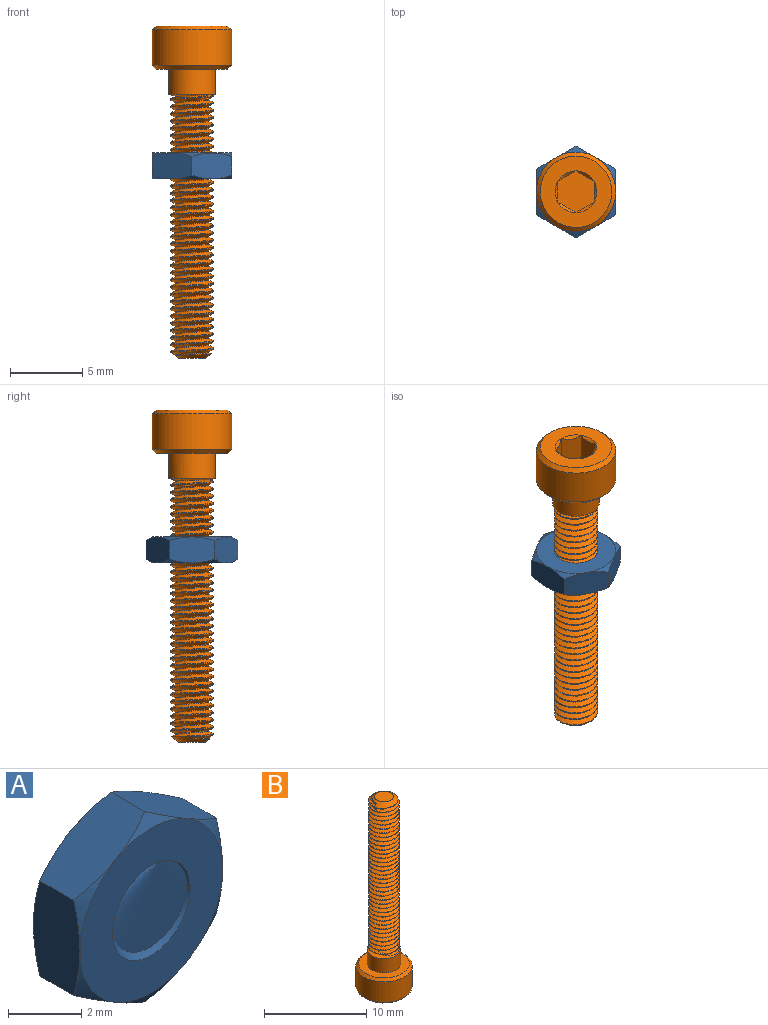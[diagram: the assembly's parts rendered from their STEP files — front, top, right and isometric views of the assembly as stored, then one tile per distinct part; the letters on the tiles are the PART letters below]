
ASSEMBLY  parts=2 mates=1
PART A: 26 faces, bbox 6.6x2.4x6.6 mm
  f0: bspline ~3.46x3mm, area 8.9mm2, adj f1,f11,f12,f19
  f1: bspline ~2.71x2.35mm, area 1.1mm2, adj f0,f2,f12,f19
  f2: bspline ~3.46x3mm, area 9.4mm2, adj f1,f11,f12,f19
  f3: plane 5.5x5.5mm, normal (0,1,0), area 16.7mm2, adj f11,f12,f13,f14,f15,f16,f17,f18
  f4: plane 3.01x2.07mm, normal (-0.5,0,-0.87), area 5.2mm2, adj f5,f9,f13,f18,f23,f24
  f5: plane 3.44x2.06mm, normal (-1,0,0), area 5.2mm2, adj f4,f6,f17,f18,f24,f25
  f6: plane 3.01x2.07mm, normal (-0.5,0,0.87), area 5.2mm2, adj f5,f7,f16,f17,f20,f25
  f7: plane 3.01x2.07mm, normal (0.5,0,0.87), area 5.2mm2, adj f6,f8,f15,f16,f20,f21
  f8: plane 3.44x2.06mm, normal (1,0,0), area 5.2mm2, adj f7,f9,f14,f15,f21,f22
  f9: plane 3.01x2.07mm, normal (0.5,0,-0.87), area 5.2mm2, adj f4,f8,f13,f14,f22,f23
  f10: plane 5.5x5.5mm, normal (0,-1,0), area 16.7mm2, adj f11,f19,f20,f21,f22,f23,f24,f25
  f11: cylinder r=1.5mm len=3mm, axis (0,-1,0), area 2.1mm2, adj f0,f2,f3,f10
  f12: cone r=1.5mm half-angle=45deg, axis (0,1,0), area 2mm2, adj f0,f1,f2,f3
  f13: cone r=2.75mm half-angle=60deg, axis (0,-1,0), area 0.7mm2, adj f3,f4,f9
  f14: cone r=2.75mm half-angle=60deg, axis (0,-1,0), area 0.7mm2, adj f3,f8,f9
  f15: cone r=2.75mm half-angle=60deg, axis (0,-1,0), area 0.7mm2, adj f3,f7,f8
  f16: cone r=2.75mm half-angle=60deg, axis (0,-1,0), area 0.7mm2, adj f3,f6,f7
  f17: cone r=2.75mm half-angle=60deg, axis (0,-1,0), area 0.7mm2, adj f3,f5,f6
  f18: cone r=2.75mm half-angle=60deg, axis (0,-1,0), area 0.7mm2, adj f3,f4,f5
  f19: cone r=1.5mm half-angle=45deg, axis (0,-1,0), area 2mm2, adj f0,f1,f2,f10
  f20: cone r=2.75mm half-angle=60deg, axis (0,1,0), area 0.7mm2, adj f6,f7,f10
  f21: cone r=2.75mm half-angle=60deg, axis (0,1,0), area 0.7mm2, adj f7,f8,f10
  f22: cone r=2.75mm half-angle=60deg, axis (0,1,0), area 0.7mm2, adj f8,f9,f10
  f23: cone r=2.75mm half-angle=60deg, axis (0,1,0), area 0.7mm2, adj f4,f9,f10
  f24: cone r=2.75mm half-angle=60deg, axis (0,1,0), area 0.7mm2, adj f4,f5,f10
  f25: cone r=2.75mm half-angle=60deg, axis (0,1,0), area 0.7mm2, adj f5,f6,f10
PART B: 27 faces, bbox 5.5x5.5x23 mm
  f0: cylinder r=1.5mm len=17.83mm, axis (0,0,1), area 0.7mm2, adj f1,f2,f4,f5,f7
  f1: bspline ~18.52x3.46mm, area 113.2mm2, adj f0,f3,f4,f7
  f2: bspline ~18.27x3.46mm, area 113.1mm2, adj f0,f3,f5,f7
  f3: cylinder r=1.18mm len=17.97mm, axis (0,0,-1), area 57.2mm2, adj f1,f2,f4,f7
  f4: cone r=0.92mm half-angle=55deg, axis (0,0,-1), area 3.5mm2, adj f0,f1,f3,f5,f6
  f5: cone r=0.92mm half-angle=55deg, axis (0,0,-1), area 0.1mm2, adj f0,f2,f4
  f6: plane 1.84x1.84mm, normal (0,0,1), area 2.7mm2, adj f4
  f7: cone r=1.63mm half-angle=75deg, axis (0,0,-1), area 2.7mm2, adj f0,f1,f2,f3,f8
  f8: cylinder r=1.63mm len=3.25mm, axis (0,0,1), area 17.7mm2, adj f7,f9
  f9: plane 4.95x4.95mm, normal (0,0,1), area 10.9mm2, adj f8,f26
  f10: cylinder r=2.75mm len=5.5mm, axis (0,0,1), area 42.3mm2, adj f25,f26
  f11: plane 4.95x4.95mm, normal (0,0,-1), area 12.7mm2, adj f12,f13,f14,f15,f16,f17,f25
  f12: cone r=1.44mm half-angle=45deg, axis (0,0,-1), area 0.3mm2, adj f11,f19
  f13: cone r=1.44mm half-angle=45deg, axis (0,0,-1), area 0.3mm2, adj f11,f20
  f14: cone r=1.44mm half-angle=45deg, axis (0,0,-1), area 0.3mm2, adj f11,f21
  f15: cone r=1.44mm half-angle=45deg, axis (0,0,-1), area 0.3mm2, adj f11,f22
  f16: cone r=1.44mm half-angle=45deg, axis (0,0,-1), area 0.3mm2, adj f11,f23
  f17: cone r=1.44mm half-angle=45deg, axis (0,0,-1), area 0.3mm2, adj f11,f24
  f18: plane 2.89x2.5mm, normal (0,0,-1), area 5.4mm2, adj f19,f20,f21,f22,f23,f24
  f19: plane 1.88x1.25mm, normal (-0.5,-0.87,0), area 2.5mm2, adj f12,f18,f20,f24
  f20: plane 1.88x1.45mm, normal (-1,0,0), area 2.5mm2, adj f13,f18,f19,f21
  f21: plane 1.88x1.25mm, normal (-0.5,0.87,0), area 2.5mm2, adj f14,f18,f20,f22
  f22: plane 1.88x1.25mm, normal (0.5,0.87,0), area 2.5mm2, adj f15,f18,f21,f23
  f23: plane 1.88x1.45mm, normal (1,0,0), area 2.5mm2, adj f16,f18,f22,f24
  f24: plane 1.88x1.25mm, normal (0.5,-0.87,0), area 2.5mm2, adj f17,f18,f19,f23
  f25: cone r=2.48mm half-angle=45deg, axis (0,0,1), area 6.4mm2, adj f10,f11
  f26: cone r=2.75mm half-angle=45deg, axis (0,0,-1), area 6.4mm2, adj f9,f10
PLACE A rot(axis=(1,0,0),90deg) t=(-17.92,-31.82,-30.26)mm
PLACE B rot(axis=(-1,0,0),180deg) t=(-17.92,-31.82,-43.56)mm
MATE cylindrical A.f11 <-> B.f0  axis (0,0,1) through (-17.92,-31.82,-29.36)mm
